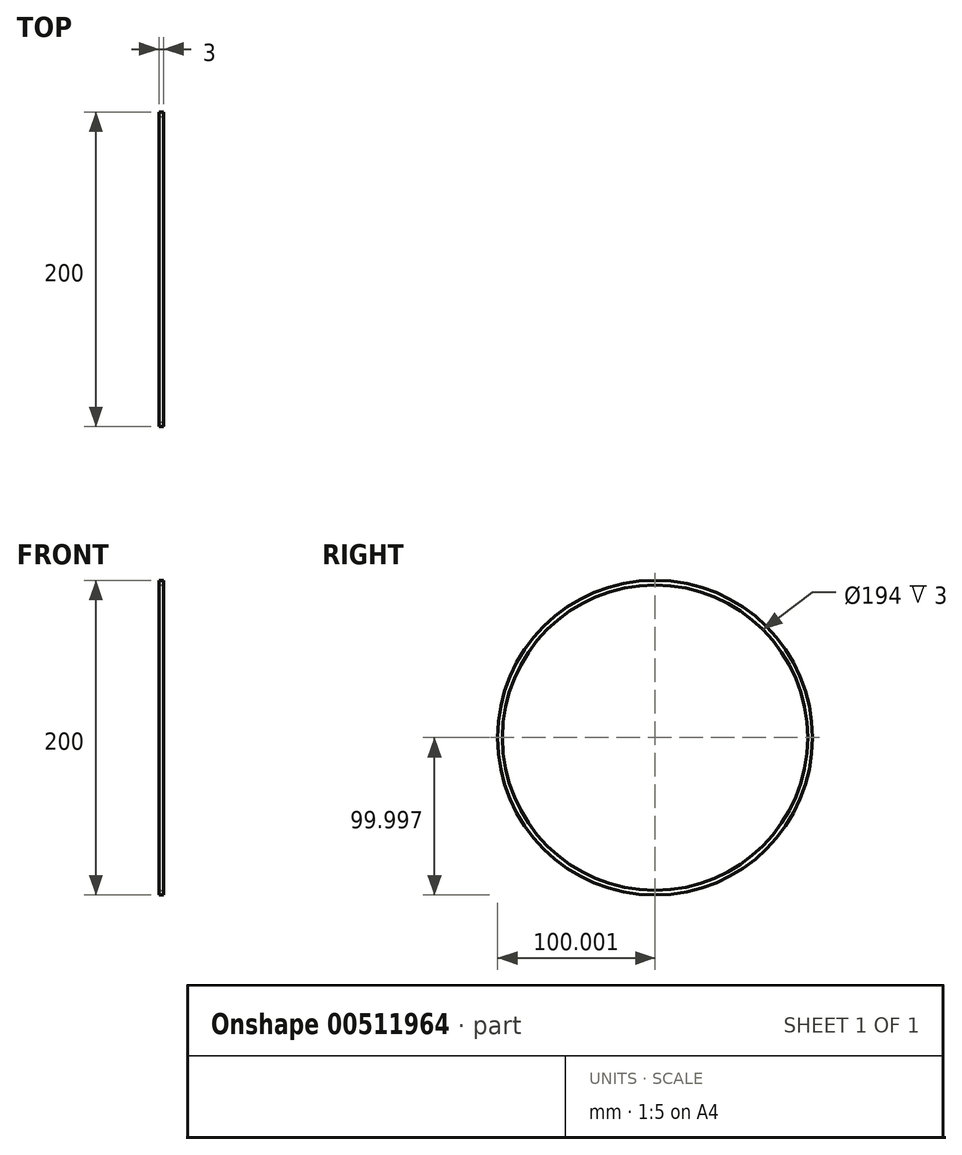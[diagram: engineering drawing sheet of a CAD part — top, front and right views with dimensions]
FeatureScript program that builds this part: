
annotation { "Feature Type Name" : "Feature", "Feature Type Description" : "" }
export const myFeature = defineFeature(function(context is Context, id is Id, definition is map)
    precondition{}
    {
        {
            var Q0;
            Q0=qCreatedBy(makeId("Right.planeOp"),FACE);
            var sketch = newSketch(context, id + "F0", { "sketchPlane" : qUnion([Q0])});
            skCircle(sketch, "E0", {"center": v(-420.6, -91.93) * mm, "radius": 100 * mm});
            skSolve(sketch);
        }
        {
            var Q0;
            Q0=qSketchRegion(id+"F0",true);
            extrude(context, id + "F1", {"entities" : qUnion([Q0]), "depth" : 3 * mm, "offsetDistance" : 25 * mm});
        }
        {
            var Q0;
            Q0=makeQuery(id+"F1.opExtrude","CAP_FACE",FACE,{"disambiguationData":[OSD([sQuery(id+"F0.wireOp",EDGE,"E0")])],"isStart":false});
            var sketch = newSketch(context, id + "F2", { "sketchPlane" : qUnion([Q0])});
            skCircle(sketch, "E1", {"center": v(-420.6, -91.93) * mm, "radius": 97 * mm});
            skSolve(sketch);
        }
        {
            var Q0;
            Q0=makeQuery(id+"F2.imprint","IMPRINT",FACE,{"disambiguationData":[TD([[makeQuery(id+"F2.imprint","IMPRINT",EDGE,{"derivedFrom":sQuery(id+"F2.wireOp",EDGE,"E1")}),1.0]])]});
            extrude(context, id + "F3", {"entities" : qUnion([Q0]), "operationType" : NewBodyOperationType.REMOVE, "oppositeDirection" : true, "depth" : 3 * mm, "offsetDistance" : 25 * mm});
        }
    });
